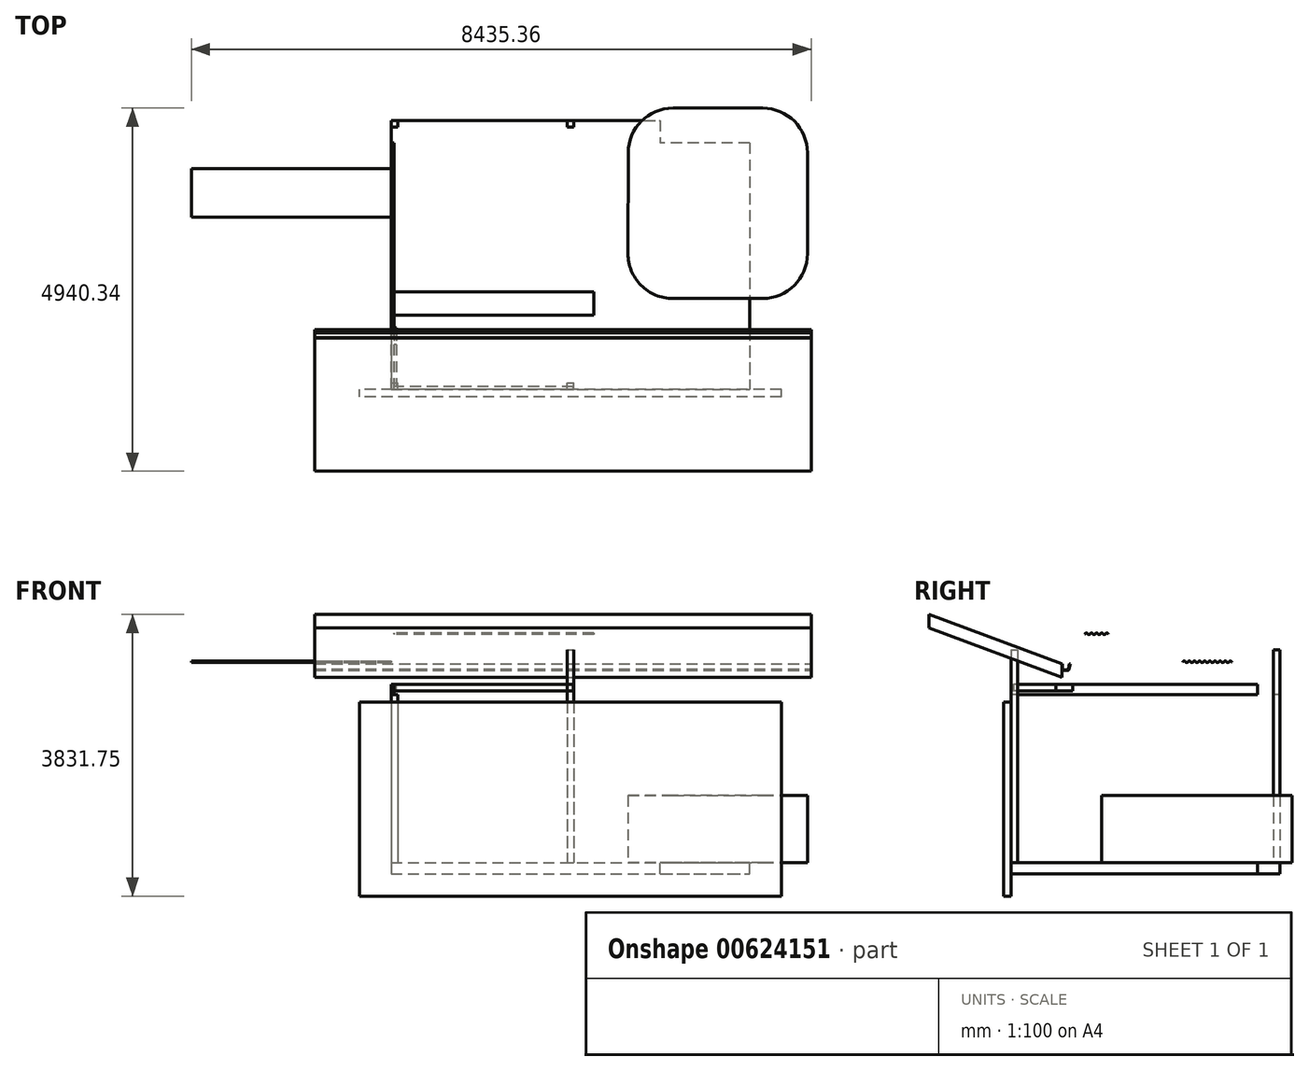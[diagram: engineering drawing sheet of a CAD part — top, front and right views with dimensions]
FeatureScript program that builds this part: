
annotation { "Feature Type Name" : "Feature", "Feature Type Description" : "" }
export const myFeature = defineFeature(function(context is Context, id is Id, definition is map)
    precondition{}
    {
        {
            var Q0;
            Q0=qCreatedBy(makeId("Top.planeOp"),FACE);
            var sketch = newSketch(context, id + "F0", { "sketchPlane" : qUnion([Q0])});
            skLineSegment(sketch, "E0.bottom", {"start": v(-2397.88, 2473.86) * mm, "end": v(2478.92, 2473.86) * mm});
            skLineSegment(sketch, "E0.top", {"start": v(-2397.88, -1183.74) * mm, "end": v(2478.92, -1183.74) * mm});
            skLineSegment(sketch, "E0.left", {"start": v(-2397.88, 2473.86) * mm, "end": v(-2397.88, -1183.74) * mm});
            skLineSegment(sketch, "E0.right", {"start": v(2478.92, 2473.86) * mm, "end": v(2478.92, -1183.74) * mm});
            skSolve(sketch);
        }
        {
            var Q0;
            Q0 = qSketchRegion(id + "F0", true);
            extrude(context, id + "F1", {"entities" : qUnion([Q0]), "depth" : 152.4 * mm, "offsetDistance" : 25.4 * mm});
        }
        {
            var Q0;
            Q0=makeQuery(id+"F1.opExtrude","CAP_FACE",FACE,{"disambiguationData":[OSD([sQuery(id+"F0.wireOp",EDGE,"E0.bottom"),sQuery(id+"F0.wireOp",EDGE,"E0.top"),sQuery(id+"F0.wireOp",EDGE,"E0.left"),sQuery(id+"F0.wireOp",EDGE,"E0.right")])],"isStart":false});
            var sketch = newSketch(context, id + "F2", { "sketchPlane" : qUnion([Q0])});
            skLineSegment(sketch, "E1.bottom", {"start": v(-2397.88, -1183.74) * mm, "end": v(-2308.98, -1183.74) * mm});
            skLineSegment(sketch, "E1.top", {"start": v(-2397.88, -1094.84) * mm, "end": v(-2308.98, -1094.84) * mm});
            skLineSegment(sketch, "E1.left", {"start": v(-2397.88, -1183.74) * mm, "end": v(-2397.88, -1094.84) * mm});
            skLineSegment(sketch, "E1.right", {"start": v(-2308.98, -1183.74) * mm, "end": v(-2308.98, -1094.84) * mm});
            skLineSegment(sketch, "E2.bottom", {"start": v(-2397.88, 2473.86) * mm, "end": v(-2308.98, 2473.86) * mm});
            skLineSegment(sketch, "E2.top", {"start": v(-2397.88, 2384.96) * mm, "end": v(-2308.98, 2384.96) * mm});
            skLineSegment(sketch, "E2.left", {"start": v(-2397.88, 2473.86) * mm, "end": v(-2397.88, 2384.96) * mm});
            skLineSegment(sketch, "E2.right", {"start": v(-2308.98, 2473.86) * mm, "end": v(-2308.98, 2384.96) * mm});
            skSolve(sketch);
        }
        {
            var Q0;
            Q0 = qSketchRegion(id + "F2", true);
            extrude(context, id + "F3", {"entities" : qUnion([Q0]), "depth" : 2286 * mm, "offsetDistance" : 25.4 * mm});
        }
        {
            var Q0;
            Q0=makeQuery(id+"F1.opExtrude","CAP_FACE",FACE,{"disambiguationData":[OSD([sQuery(id+"F0.wireOp",EDGE,"E0.bottom"),sQuery(id+"F0.wireOp",EDGE,"E0.top"),sQuery(id+"F0.wireOp",EDGE,"E0.left"),sQuery(id+"F0.wireOp",EDGE,"E0.right")])],"isStart":false});
            var sketch = newSketch(context, id + "F4", { "sketchPlane" : qUnion([Q0])});
            skLineSegment(sketch, "E3.bottom", {"start": v(-3.93, -1183.74) * mm, "end": v(84.97, -1183.74) * mm});
            skLineSegment(sketch, "E3.top", {"start": v(-3.93, -1094.84) * mm, "end": v(84.97, -1094.84) * mm});
            skLineSegment(sketch, "E3.left", {"start": v(-3.93, -1183.74) * mm, "end": v(-3.93, -1094.84) * mm});
            skLineSegment(sketch, "E3.right", {"start": v(84.97, -1183.74) * mm, "end": v(84.97, -1094.84) * mm});
            skLineSegment(sketch, "E4.bottom", {"start": v(84.97, 2384.96) * mm, "end": v(-3.93, 2384.96) * mm});
            skLineSegment(sketch, "E4.top", {"start": v(84.97, 2473.86) * mm, "end": v(-3.93, 2473.86) * mm});
            skLineSegment(sketch, "E4.left", {"start": v(84.97, 2384.96) * mm, "end": v(84.97, 2473.86) * mm});
            skLineSegment(sketch, "E4.right", {"start": v(-3.93, 2384.96) * mm, "end": v(-3.93, 2473.86) * mm});
            skSolve(sketch);
        }
        {
            var Q0;
            Q0 = qSketchRegion(id + "F4", true);
            extrude(context, id + "F5", {"entities" : qUnion([Q0]), "depth" : 2895.6 * mm, "offsetDistance" : 25.4 * mm});
        }
        {
            var Q0;
            Q0=makeQuery(id+"F3.opExtrude","CAP_FACE",FACE,{"disambiguationData":[OSD([sQuery(id+"F2.wireOp",EDGE,"E1.bottom"),sQuery(id+"F2.wireOp",EDGE,"E1.top"),sQuery(id+"F2.wireOp",EDGE,"E1.left"),sQuery(id+"F2.wireOp",EDGE,"E1.right")])],"isStart":false});
            var sketch = newSketch(context, id + "F6", { "sketchPlane" : qUnion([Q0])});
            skLineSegment(sketch, "E5.bottom", {"start": v(-2359.78, -1183.74) * mm, "end": v(-2397.88, -1183.74) * mm});
            skLineSegment(sketch, "E5.right", {"start": v(-2397.88, -1183.74) * mm, "end": v(-2397.88, 2169.06) * mm});
            skLineSegment(sketch, "E6", {"start": v(-2359.78, -1183.74) * mm, "end": v(-2359.78, 2169.06) * mm});
            skLineSegment(sketch, "E7", {"start": v(-2397.88, 2169.06) * mm, "end": v(-2359.78, 2169.06) * mm});
            skSolve(sketch);
        }
        {
            var Q0;
            Q0 = qSketchRegion(id + "F6", true);
            extrude(context, id + "F7", {"entities" : qUnion([Q0]), "depth" : 139.7 * mm, "offsetDistance" : 25.4 * mm});
        }
        {
            var Q0;
            Q0=makeQuery(id+"F7.opExtrude","SWEPT_FACE",FACE,{"disambiguationData":[OSD([sQuery(id+"F6.wireOp",EDGE,"E5.right")])]});
            var sketch = newSketch(context, id + "F8", { "sketchPlane" : qUnion([Q0])});
            skArc(sketch, "E8", {"start": v(-1781.99, 2877.56) * mm, "mid": v(-1781.99, 2877.67) * mm, "end": v(-1781.99, 2877.79) * mm});
            skArc(sketch, "E9.1.0.0", {"start": v(-1715, 2888.18) * mm, "mid": v(-1732.46, 2898.1) * mm, "end": v(-1749.92, 2888.18) * mm});
            skArc(sketch, "E9.2.0.0", {"start": v(-1645.15, 2888.18) * mm, "mid": v(-1662.6, 2898.1) * mm, "end": v(-1680.07, 2888.18) * mm});
            skArc(sketch, "E9.3.0.0", {"start": v(-1575.3, 2888.18) * mm, "mid": v(-1592.76, 2898.1) * mm, "end": v(-1610.22, 2888.18) * mm});
            skArc(sketch, "E9.4.0.0", {"start": v(-1505.45, 2888.18) * mm, "mid": v(-1522.9, 2898.1) * mm, "end": v(-1540.37, 2888.18) * mm});
            skArc(sketch, "E9.5.0.0", {"start": v(-1435.6, 2888.18) * mm, "mid": v(-1453.06, 2898.1) * mm, "end": v(-1470.52, 2888.18) * mm});
            skArc(sketch, "E9.6.0.0", {"start": v(-1365.75, 2888.18) * mm, "mid": v(-1383.2, 2898.1) * mm, "end": v(-1400.67, 2888.18) * mm});
            skArc(sketch, "E9.7.0.0", {"start": v(-1295.9, 2888.18) * mm, "mid": v(-1313.36, 2898.1) * mm, "end": v(-1330.82, 2888.18) * mm});
            skArc(sketch, "E9.8.0.0", {"start": v(-1226.05, 2888.18) * mm, "mid": v(-1243.5, 2898.1) * mm, "end": v(-1260.97, 2888.18) * mm});
            skArc(sketch, "E9.9.0.0", {"start": v(-1156.2, 2888.18) * mm, "mid": v(-1173.66, 2898.1) * mm, "end": v(-1191.12, 2888.18) * mm});
            skLineSegment(sketch, "E9.direction1", {"start": v(-1802.3, 2877.79) * mm, "end": v(-1732.46, 2877.79) * mm, "construction": true});
            skArc(sketch, "E10", {"start": v(-1784.85, 2888.18) * mm, "mid": v(-1767.38, 2878.25) * mm, "end": v(-1749.92, 2888.18) * mm});
            skArc(sketch, "E11.1.0.0", {"start": v(-1715, 2888.18) * mm, "mid": v(-1697.53, 2878.25) * mm, "end": v(-1680.07, 2888.18) * mm});
            skArc(sketch, "E11.2.0.0", {"start": v(-1645.15, 2888.18) * mm, "mid": v(-1627.68, 2878.25) * mm, "end": v(-1610.22, 2888.18) * mm});
            skArc(sketch, "E11.3.0.0", {"start": v(-1575.3, 2888.18) * mm, "mid": v(-1557.83, 2878.25) * mm, "end": v(-1540.37, 2888.18) * mm});
            skArc(sketch, "E11.4.0.0", {"start": v(-1505.45, 2888.18) * mm, "mid": v(-1487.98, 2878.25) * mm, "end": v(-1470.52, 2888.18) * mm});
            skArc(sketch, "E11.5.0.0", {"start": v(-1435.6, 2888.18) * mm, "mid": v(-1418.13, 2878.25) * mm, "end": v(-1400.67, 2888.18) * mm});
            skArc(sketch, "E11.6.0.0", {"start": v(-1365.75, 2888.18) * mm, "mid": v(-1348.28, 2878.25) * mm, "end": v(-1330.82, 2888.18) * mm});
            skArc(sketch, "E11.7.0.0", {"start": v(-1295.9, 2888.18) * mm, "mid": v(-1278.43, 2878.25) * mm, "end": v(-1260.97, 2888.18) * mm});
            skArc(sketch, "E11.8.0.0", {"start": v(-1226.05, 2888.18) * mm, "mid": v(-1208.58, 2878.25) * mm, "end": v(-1191.12, 2888.18) * mm});
            skLineSegment(sketch, "E11.direction1", {"start": v(-1767.38, 2898.57) * mm, "end": v(-1697.53, 2898.57) * mm, "construction": true});
            skArc(sketch, "E12.trimOffspring", {"start": v(-1752.78, 2877.79) * mm, "mid": v(-1752.78, 2877.67) * mm, "end": v(-1752.78, 2877.56) * mm});
            skArc(sketch, "E13.trimOffspring", {"start": v(-1784.85, 2888.18) * mm, "mid": v(-1802.67, 2898.1) * mm, "end": v(-1820.13, 2887.55) * mm});
            skArc(sketch, "E14.0.11.0", {"start": v(-1013.64, 2877.56) * mm, "mid": v(-1013.64, 2877.67) * mm, "end": v(-1013.64, 2877.79) * mm});
            skArc(sketch, "E15.0", {"start": v(-1785.94, 2887.53) * mm, "mid": v(-1802.65, 2896.83) * mm, "end": v(-1819.01, 2886.94) * mm});
            skArc(sketch, "E15.1", {"start": v(-1785.94, 2887.53) * mm, "mid": v(-1767.38, 2876.98) * mm, "end": v(-1748.83, 2887.53) * mm});
            skArc(sketch, "E15.2", {"start": v(-1716.09, 2887.53) * mm, "mid": v(-1732.46, 2896.84) * mm, "end": v(-1748.83, 2887.53) * mm});
            skArc(sketch, "E15.3", {"start": v(-1716.09, 2887.53) * mm, "mid": v(-1697.53, 2876.98) * mm, "end": v(-1678.98, 2887.53) * mm});
            skArc(sketch, "E15.4", {"start": v(-1646.24, 2887.53) * mm, "mid": v(-1662.6, 2896.84) * mm, "end": v(-1678.98, 2887.53) * mm});
            skArc(sketch, "E15.5", {"start": v(-1646.24, 2887.53) * mm, "mid": v(-1627.68, 2876.98) * mm, "end": v(-1609.13, 2887.53) * mm});
            skArc(sketch, "E15.6", {"start": v(-1576.39, 2887.53) * mm, "mid": v(-1592.76, 2896.84) * mm, "end": v(-1609.13, 2887.53) * mm});
            skArc(sketch, "E15.7", {"start": v(-1576.39, 2887.53) * mm, "mid": v(-1557.83, 2876.98) * mm, "end": v(-1539.28, 2887.53) * mm});
            skArc(sketch, "E15.8", {"start": v(-1506.54, 2887.53) * mm, "mid": v(-1522.9, 2896.84) * mm, "end": v(-1539.28, 2887.53) * mm});
            skArc(sketch, "E15.9", {"start": v(-1296.99, 2887.53) * mm, "mid": v(-1278.43, 2876.98) * mm, "end": v(-1259.88, 2887.53) * mm});
            skArc(sketch, "E15.10", {"start": v(-1227.14, 2887.53) * mm, "mid": v(-1243.5, 2896.84) * mm, "end": v(-1259.88, 2887.53) * mm});
            skArc(sketch, "E15.11", {"start": v(-1227.14, 2887.53) * mm, "mid": v(-1208.58, 2876.98) * mm, "end": v(-1190.03, 2887.53) * mm});
            skArc(sketch, "E15.12", {"start": v(-1157.29, 2887.53) * mm, "mid": v(-1173.66, 2896.84) * mm, "end": v(-1190.03, 2887.53) * mm});
            skArc(sketch, "E15.13", {"start": v(-1296.99, 2887.53) * mm, "mid": v(-1313.36, 2896.84) * mm, "end": v(-1329.73, 2887.53) * mm});
            skArc(sketch, "E15.14", {"start": v(-1366.84, 2887.53) * mm, "mid": v(-1348.28, 2876.98) * mm, "end": v(-1329.73, 2887.53) * mm});
            skArc(sketch, "E15.15", {"start": v(-1366.84, 2887.53) * mm, "mid": v(-1383.2, 2896.84) * mm, "end": v(-1399.58, 2887.53) * mm});
            skArc(sketch, "E15.16", {"start": v(-1436.69, 2887.53) * mm, "mid": v(-1418.13, 2876.98) * mm, "end": v(-1399.58, 2887.53) * mm});
            skArc(sketch, "E15.17", {"start": v(-1436.69, 2887.53) * mm, "mid": v(-1453.06, 2896.84) * mm, "end": v(-1469.43, 2887.53) * mm});
            skArc(sketch, "E15.18", {"start": v(-1506.54, 2887.53) * mm, "mid": v(-1487.98, 2876.98) * mm, "end": v(-1469.43, 2887.53) * mm});
            skLineSegment(sketch, "E16", {"start": v(-1820.13, 2887.55) * mm, "end": v(-1819.01, 2886.94) * mm});
            skLineSegment(sketch, "E17", {"start": v(-1157.29, 2887.53) * mm, "end": v(-1156.2, 2888.18) * mm});
            skSolve(sketch);
        }
        {
            var Q0;
            Q0=makeQuery(id+"F8.imprint","IMPRINT",FACE,{"disambiguationData":[TD([[makeQuery(id+"F8.imprint","IMPRINT",EDGE,{"derivedFrom":sQuery(id+"F8.wireOp",EDGE,"E9.1.0.0")}),1.0]])]});
            extrude(context, id + "F9", {"entities" : qUnion([Q0]), "depth" : 2717.8 * mm, "offsetDistance" : 25.4 * mm});
        }
        {
            var Q0;
            Q0=makeQuery(id+"F7.opExtrude","SWEPT_FACE",FACE,{"disambiguationData":[OSD([sQuery(id+"F6.wireOp",EDGE,"E6")])]});
            var sketch = newSketch(context, id + "F10", { "sketchPlane" : qUnion([Q0])});
            skLineSegment(sketch, "E18", {"start": v(-1183.74, 2578.1) * mm, "end": v(-1145.64, 2578.1) * mm});
            skLineSegment(sketch, "E19", {"start": v(-1145.64, 2578.1) * mm, "end": v(-1145.64, 2489.2) * mm});
            skLineSegment(sketch, "E20", {"start": v(-1145.64, 2489.2) * mm, "end": v(-1183.74, 2489.2) * mm});
            skLineSegment(sketch, "E21", {"start": v(-1183.74, 2489.2) * mm, "end": v(-1183.74, 2578.1) * mm});
            skSolve(sketch);
        }
        {
            var Q0;
            Q0=makeQuery(id+"F10.imprint","IMPRINT",FACE,{"disambiguationData":[TD([[makeQuery(id+"F10.imprint","IMPRINT",EDGE,{"derivedFrom":sQuery(id+"F10.wireOp",EDGE,"E18")}),-1.0]])]});
            extrude(context, id + "F11", {"entities" : qUnion([Q0]), "depth" : 2438.4 * mm, "offsetDistance" : 25.4 * mm});
        }
        {
            var Q0;
            Q0=makeQuery(id+"F11.opExtrude","SWEPT_FACE",FACE,{"disambiguationData":[OSD([sQuery(id+"F10.wireOp",EDGE,"E19")])]});
            var sketch = newSketch(context, id + "F12", { "sketchPlane" : qUnion([Q0])});
            skLineSegment(sketch, "E22", {"start": v(2359.78, 2578.1) * mm, "end": v(2359.78, 2489.2) * mm});
            skLineSegment(sketch, "E23", {"start": v(2359.78, 2489.2) * mm, "end": v(2321.68, 2489.2) * mm});
            skLineSegment(sketch, "E24", {"start": v(2321.68, 2489.2) * mm, "end": v(2321.68, 2578.1) * mm});
            skLineSegment(sketch, "E25", {"start": v(2321.68, 2578.1) * mm, "end": v(2359.78, 2578.1) * mm});
            skSolve(sketch);
        }
        {
            var Q0;
            Q0 = qSketchRegion(id + "F12", true);
            extrude(context, id + "F13", {"entities" : qUnion([Q0]), "depth" : 571.5 * mm, "offsetDistance" : 25.4 * mm});
        }
        {
            var Q0;
            Q0=makeQuery(id+"F13.opExtrude","CAP_FACE",FACE,{"disambiguationData":[OSD([sQuery(id+"F12.wireOp",EDGE,"E22"),sQuery(id+"F12.wireOp",EDGE,"E23"),sQuery(id+"F12.wireOp",EDGE,"E24"),sQuery(id+"F12.wireOp",EDGE,"E25")])],"isStart":false});
            var sketch = newSketch(context, id + "F14", { "sketchPlane" : qUnion([Q0])});
            skLineSegment(sketch, "E26", {"start": v(2321.68, 2578.1) * mm, "end": v(2321.68, 2489.2) * mm});
            skLineSegment(sketch, "E27", {"start": v(2321.68, 2489.2) * mm, "end": v(2359.78, 2489.2) * mm});
            skLineSegment(sketch, "E28", {"start": v(2359.78, 2489.2) * mm, "end": v(2359.78, 2578.1) * mm});
            skLineSegment(sketch, "E29", {"start": v(2359.78, 2578.1) * mm, "end": v(2321.68, 2578.1) * mm});
            skSolve(sketch);
        }
        {
            var Q0;
            Q0 = qSketchRegion(id + "F14", true);
            extrude(context, id + "F15", {"entities" : qUnion([Q0]), "depth" : 228.6 * mm, "offsetDistance" : 25.4 * mm});
        }
        {
            var Q0;
            Q0=makeQuery(id+"F7.opExtrude","SWEPT_FACE",FACE,{"disambiguationData":[OSD([sQuery(id+"F6.wireOp",EDGE,"E6")])]});
            var sketch = newSketch(context, id + "F16", { "sketchPlane" : qUnion([Q0])});
            skArc(sketch, "E30", {"start": v(-137.52, 3257.84) * mm, "mid": v(-137.51, 3257.96) * mm, "end": v(-137.51, 3258.07) * mm});
            skArc(sketch, "E31.1.0.0", {"start": v(-70.52, 3268.46) * mm, "mid": v(-87.98, 3278.39) * mm, "end": v(-105.45, 3268.46) * mm});
            skArc(sketch, "E31.2.0.0", {"start": v(-0.67, 3268.46) * mm, "mid": v(-18.13, 3278.39) * mm, "end": v(-35.6, 3268.46) * mm});
            skArc(sketch, "E31.3.0.0", {"start": v(69.18, 3268.46) * mm, "mid": v(51.72, 3278.39) * mm, "end": v(34.25, 3268.46) * mm});
            skArc(sketch, "E31.4.0.0", {"start": v(139.03, 3268.46) * mm, "mid": v(121.57, 3278.39) * mm, "end": v(104.1, 3268.46) * mm});
            skLineSegment(sketch, "E31.direction1", {"start": v(-157.83, 3258.07) * mm, "end": v(-87.98, 3258.07) * mm, "construction": true});
            skArc(sketch, "E32", {"start": v(-140.37, 3268.46) * mm, "mid": v(-122.9, 3258.53) * mm, "end": v(-105.45, 3268.46) * mm});
            skArc(sketch, "E33.1.0.0", {"start": v(-70.52, 3268.46) * mm, "mid": v(-53.06, 3258.53) * mm, "end": v(-35.6, 3268.46) * mm});
            skArc(sketch, "E33.2.0.0", {"start": v(-0.67, 3268.46) * mm, "mid": v(16.8, 3258.53) * mm, "end": v(34.25, 3268.46) * mm});
            skArc(sketch, "E33.3.0.0", {"start": v(69.18, 3268.46) * mm, "mid": v(86.64, 3258.53) * mm, "end": v(104.1, 3268.46) * mm});
            skLineSegment(sketch, "E33.direction1", {"start": v(-122.9, 3278.85) * mm, "end": v(-53.06, 3278.85) * mm, "construction": true});
            skArc(sketch, "E34.trimOffspring", {"start": v(-108.3, 3258.07) * mm, "mid": v(-108.3, 3257.96) * mm, "end": v(-108.3, 3257.84) * mm});
            skArc(sketch, "E35.trimOffspring", {"start": v(-140.37, 3268.46) * mm, "mid": v(-158.2, 3278.39) * mm, "end": v(-175.65, 3267.83) * mm});
            skArc(sketch, "E36.0.11.0", {"start": v(630.83, 3257.84) * mm, "mid": v(630.84, 3257.96) * mm, "end": v(630.84, 3258.07) * mm});
            skArc(sketch, "E37.0", {"start": v(-141.46, 3267.8) * mm, "mid": v(-158.17, 3277.12) * mm, "end": v(-174.54, 3267.22) * mm});
            skArc(sketch, "E37.1", {"start": v(-141.46, 3267.8) * mm, "mid": v(-122.9, 3257.26) * mm, "end": v(-104.36, 3267.8) * mm});
            skArc(sketch, "E37.2", {"start": v(-71.61, 3267.8) * mm, "mid": v(-87.98, 3277.12) * mm, "end": v(-104.36, 3267.8) * mm});
            skArc(sketch, "E37.3", {"start": v(-71.61, 3267.8) * mm, "mid": v(-53.06, 3257.26) * mm, "end": v(-34.5, 3267.8) * mm});
            skArc(sketch, "E37.4", {"start": v(-1.76, 3267.8) * mm, "mid": v(-18.13, 3277.12) * mm, "end": v(-34.5, 3267.8) * mm});
            skArc(sketch, "E37.5", {"start": v(-1.76, 3267.8) * mm, "mid": v(16.8, 3257.26) * mm, "end": v(35.34, 3267.8) * mm});
            skArc(sketch, "E37.6", {"start": v(68.09, 3267.8) * mm, "mid": v(51.72, 3277.12) * mm, "end": v(35.34, 3267.8) * mm});
            skArc(sketch, "E37.7", {"start": v(68.09, 3267.8) * mm, "mid": v(86.64, 3257.26) * mm, "end": v(105.2, 3267.8) * mm});
            skArc(sketch, "E37.8", {"start": v(137.94, 3267.8) * mm, "mid": v(121.57, 3277.12) * mm, "end": v(105.2, 3267.8) * mm});
            skLineSegment(sketch, "E38", {"start": v(-175.65, 3267.83) * mm, "end": v(-174.54, 3267.22) * mm});
            skLineSegment(sketch, "E39", {"start": v(139.03, 3268.46) * mm, "end": v(137.94, 3267.8) * mm});
            skSolve(sketch);
        }
        {
            var Q0;
            Q0=makeQuery(id+"F16.imprint","IMPRINT",FACE,{"disambiguationData":[TD([[makeQuery(id+"F16.imprint","IMPRINT",EDGE,{"derivedFrom":sQuery(id+"F16.wireOp",EDGE,"E31.1.0.0")}),1.0]])]});
            extrude(context, id + "F17", {"entities" : qUnion([Q0]), "depth" : 2717.8 * mm, "offsetDistance" : 25.4 * mm});
        }
        {
            var Q0;
            Q0=makeQuery(id+"F1.opExtrude","SWEPT_FACE",FACE,{"disambiguationData":[OSD([sQuery(id+"F0.wireOp",EDGE,"E0.top")])]});
            var sketch = newSketch(context, id + "F18", { "sketchPlane" : qUnion([Q0])});
            skLineSegment(sketch, "E40", {"start": v(-2397.88, -301.14) * mm, "end": v(2913.28, -301.14) * mm});
            skLineSegment(sketch, "E41", {"start": v(2913.28, -301.14) * mm, "end": v(2913.28, 2339.07) * mm});
            skLineSegment(sketch, "E42", {"start": v(-2397.88, -301.14) * mm, "end": v(-2826.13, -301.14) * mm});
            skLineSegment(sketch, "E43", {"start": v(-2826.13, -301.14) * mm, "end": v(-2826.13, 2339.07) * mm});
            skPoint(sketch, "E44.orphan", {"position": v(-2397.88, 3146.18) * mm});
            skLineSegment(sketch, "E45", {"start": v(2913.28, 2339.07) * mm, "end": v(-2826.13, 2339.07) * mm});
            skSolve(sketch);
        }
        {
            var Q0;
            Q0=makeQuery(id+"F18.imprint","IMPRINT",FACE,{"disambiguationData":[TD([[makeQuery(id+"F18.imprint","IMPRINT",EDGE,{"derivedFrom":sQuery(id+"F18.wireOp",EDGE,"E40")}),1.0]])]});
            var Q1;
            {var subQ0=sQuery(id+"F0.wireOp",EDGE,"E0.top");Q1=makeQuery(id+"F18.imprint","IMPRINT",FACE,{"disambiguationData":[TD([[makeQuery(id+"F18.imprint","IMPRINT",EDGE,{"derivedFrom":makeQuery(id+"F1.opExtrude","CAP_EDGE",EDGE,{"disambiguationData":[OSD([subQ0])],"isStart":true})}),1.0]])]});}
            extrude(context, id + "F19", {"entities" : qUnion([Q0, Q1]), "depth" : 101.6 * mm, "offsetDistance" : 25.4 * mm});
        }
        {
            var Q0;
            Q0=makeQuery(id+"F19.opExtrude","SWEPT_FACE",FACE,{"disambiguationData":[OSD([sQuery(id+"F18.wireOp",EDGE,"E41")])]});
            var sketch = newSketch(context, id + "F20", { "sketchPlane" : qUnion([Q0])});
            skLineSegment(sketch, "E46", {"start": v(-2299.3, 3351.64) * mm, "end": v(-489.15, 2678.41) * mm});
            skLineSegment(sketch, "E47", {"start": v(-489.15, 2678.41) * mm, "end": v(-489.15, 2857.38) * mm});
            skLineSegment(sketch, "E48", {"start": v(-489.15, 2857.38) * mm, "end": v(-2299.3, 3530.61) * mm});
            skLineSegment(sketch, "E49", {"start": v(-2299.3, 3530.61) * mm, "end": v(-2299.3, 3351.64) * mm});
            skSolve(sketch);
        }
        {
            var Q0;
            Q0 = qSketchRegion(id + "F20", true);
            extrude(context, id + "F21", {"entities" : qUnion([Q0]), "oppositeDirection" : true, "depth" : 6350 * mm, "offsetDistance" : 25.4 * mm, "hasSecondDirection" : true, "secondDirectionOppositeDirection" : false, "secondDirectionDepth" : 406.4 * mm});
        }
        {
            var Q0;
            Q0=makeQuery(id+"F21.opExtrude","CAP_FACE",FACE,{"disambiguationData":[OSD([sQuery(id+"F20.wireOp",EDGE,"E46"),sQuery(id+"F20.wireOp",EDGE,"E47"),sQuery(id+"F20.wireOp",EDGE,"E48"),sQuery(id+"F20.wireOp",EDGE,"E49")])],"isStart":true});
            var sketch = newSketch(context, id + "F22", { "sketchPlane" : qUnion([Q0])});
            skLineSegment(sketch, "E50", {"start": v(-489.15, 2791.57) * mm, "end": v(-489.15, 2857.38) * mm});
            skLineSegment(sketch, "E51", {"start": v(-489.15, 2857.38) * mm, "end": v(-480.52, 2857.38) * mm});
            skLineSegment(sketch, "E52", {"start": v(-480.52, 2857.38) * mm, "end": v(-480.52, 2790) * mm});
            skLineSegment(sketch, "E53", {"start": v(-384.66, 2857.38) * mm, "end": v(-399.5, 2789.41) * mm});
            skArc(sketch, "E54", {"start": v(-418.4, 2776.16) * mm, "mid": v(-406.36, 2779.1) * mm, "end": v(-399.5, 2789.41) * mm});
            skLineSegment(sketch, "E55", {"start": v(-465.56, 2776.45) * mm, "end": v(-418.4, 2776.16) * mm});
            skLineSegment(sketch, "E56", {"start": v(-376.36, 2857.38) * mm, "end": v(-391.57, 2787.68) * mm});
            skArc(sketch, "E57", {"start": v(-465.56, 2776.45) * mm, "mid": v(-475.63, 2780.37) * mm, "end": v(-480.52, 2790) * mm});
            skArc(sketch, "E58", {"start": v(-489.15, 2791.57) * mm, "mid": v(-482.21, 2774.83) * mm, "end": v(-465.47, 2767.9) * mm});
            skArc(sketch, "E59", {"start": v(-416.14, 2767.9) * mm, "mid": v(-400.37, 2773.46) * mm, "end": v(-391.57, 2787.68) * mm});
            skLineSegment(sketch, "E60.trimOffspring", {"start": v(-416.14, 2767.9) * mm, "end": v(-465.47, 2767.9) * mm});
            skPoint(sketch, "E61.start.orphan", {"position": v(-376.36, 2767.9) * mm});
            skPoint(sketch, "E62.start.orphan", {"position": v(-376.36, 2678.41) * mm});
            skPoint(sketch, "E63.orphan", {"position": v(-489.15, 2678.41) * mm});
            skPoint(sketch, "E64.orphan", {"position": v(-489.15, 2767.9) * mm});
            skLineSegment(sketch, "E65.trimOffspring", {"start": v(-384.66, 2857.38) * mm, "end": v(-376.36, 2857.38) * mm});
            skSolve(sketch);
        }
        {
            var Q0;
            Q0 = qSketchRegion(id + "F22", true);
            extrude(context, id + "F23", {"entities" : qUnion([Q0]), "oppositeDirection" : true, "depth" : 6756.4 * mm, "offsetDistance" : 25.4 * mm});
        }
        {
            var Q0;
            Q0=makeQuery(id+"F1.opExtrude","CAP_FACE",FACE,{"disambiguationData":[OSD([sQuery(id+"F0.wireOp",EDGE,"E0.bottom"),sQuery(id+"F0.wireOp",EDGE,"E0.top"),sQuery(id+"F0.wireOp",EDGE,"E0.left"),sQuery(id+"F0.wireOp",EDGE,"E0.right")])],"isStart":false});
            var sketch = newSketch(context, id + "F24", { "sketchPlane" : qUnion([Q0])});
            skLineSegment(sketch, "E66.bottom", {"start": v(2478.92, 2473.86) * mm, "end": v(1259.72, 2473.86) * mm});
            skLineSegment(sketch, "E66.top", {"start": v(2478.92, 2169.06) * mm, "end": v(1259.72, 2169.06) * mm});
            skLineSegment(sketch, "E66.left", {"start": v(2478.92, 2473.86) * mm, "end": v(2478.92, 2169.06) * mm});
            skLineSegment(sketch, "E66.right", {"start": v(1259.72, 2473.86) * mm, "end": v(1259.72, 2169.06) * mm});
            skSolve(sketch);
        }
        {
            var Q0;
            Q0=makeQuery(id+"F24.imprint","IMPRINT",FACE,{"disambiguationData":[TD([[makeQuery(id+"F24.imprint","IMPRINT",EDGE,{"derivedFrom":sQuery(id+"F24.wireOp",EDGE,"E66.bottom")}),-1.0]])]});
            extrude(context, id + "F25", {"entities" : qUnion([Q0]), "operationType" : NewBodyOperationType.REMOVE, "endBound" : BoundingType.UP_TO_NEXT, "oppositeDirection" : true, "depth" : 25.4 * mm, "offsetDistance" : 25.4 * mm});
        }
        {
            var Q0;
            Q0=makeQuery(id+"F1.opExtrude","CAP_FACE",FACE,{"disambiguationData":[OSD([sQuery(id+"F0.wireOp",EDGE,"E0.bottom"),sQuery(id+"F0.wireOp",EDGE,"E0.top"),sQuery(id+"F0.wireOp",EDGE,"E0.left"),sQuery(id+"F0.wireOp",EDGE,"E0.right")])],"isStart":false});
            var sketch = newSketch(context, id + "F26", { "sketchPlane" : qUnion([Q0])});
            skLineSegment(sketch, "E67", {"start": v(1438.09, 2641.05) * mm, "end": v(2658.39, 2641.05) * mm});
            skLineSegment(sketch, "E68", {"start": v(3267.99, 2031.45) * mm, "end": v(3267.99, 659.85) * mm});
            skLineSegment(sketch, "E69", {"start": v(2658.39, 50.25) * mm, "end": v(1435.61, 50.25) * mm});
            skLineSegment(sketch, "E70", {"start": v(826.01, 660.95) * mm, "end": v(828.49, 2032.55) * mm});
            skPoint(sketch, "E71.visualSharp", {"position": v(829.59, 2641.05) * mm});
            skArc(sketch, "E71.filletArc", {"start": v(1438.09, 2641.05) * mm, "mid": v(1007.42, 2462.89) * mm, "end": v(828.49, 2032.55) * mm});
            skPoint(sketch, "E72.visualSharp", {"position": v(3267.99, 2641.05) * mm});
            skArc(sketch, "E72.filletArc", {"start": v(3267.99, 2031.45) * mm, "mid": v(3089.44, 2462.5) * mm, "end": v(2658.39, 2641.05) * mm});
            skPoint(sketch, "E73.visualSharp", {"position": v(3267.99, 50.25) * mm});
            skArc(sketch, "E73.filletArc", {"start": v(2658.39, 50.25) * mm, "mid": v(3089.44, 228.8) * mm, "end": v(3267.99, 659.85) * mm});
            skPoint(sketch, "E74.visualSharp", {"position": v(824.91, 50.25) * mm});
            skArc(sketch, "E74.filletArc", {"start": v(826.01, 660.95) * mm, "mid": v(1004.17, 229.18) * mm, "end": v(1435.61, 50.25) * mm});
            skSolve(sketch);
        }
        {
            var Q0;
            {var subQ7=sQuery(id+"F26.wireOp",EDGE,"E67");Q0=makeQuery(id+"F26.imprint","IMPRINT",FACE,{"disambiguationData":[TD([[makeQuery(id+"F26.imprint","IMPRINT",EDGE,{"derivedFrom":subQ7}),-1.0]])]});}
            var Q1;
            {var subQ1=sQuery(id+"F26.wireOp",EDGE,"E70");Q1=makeQuery(id+"F26.imprint","IMPRINT",FACE,{"disambiguationData":[TD([[makeQuery(id+"F26.imprint","IMPRINT",EDGE,{"derivedFrom":subQ1}),-1.0]])]});}
            extrude(context, id + "F27", {"entities" : qUnion([Q0, Q1]), "depth" : 914.4 * mm, "offsetDistance" : 25.4 * mm});
        }
    });
